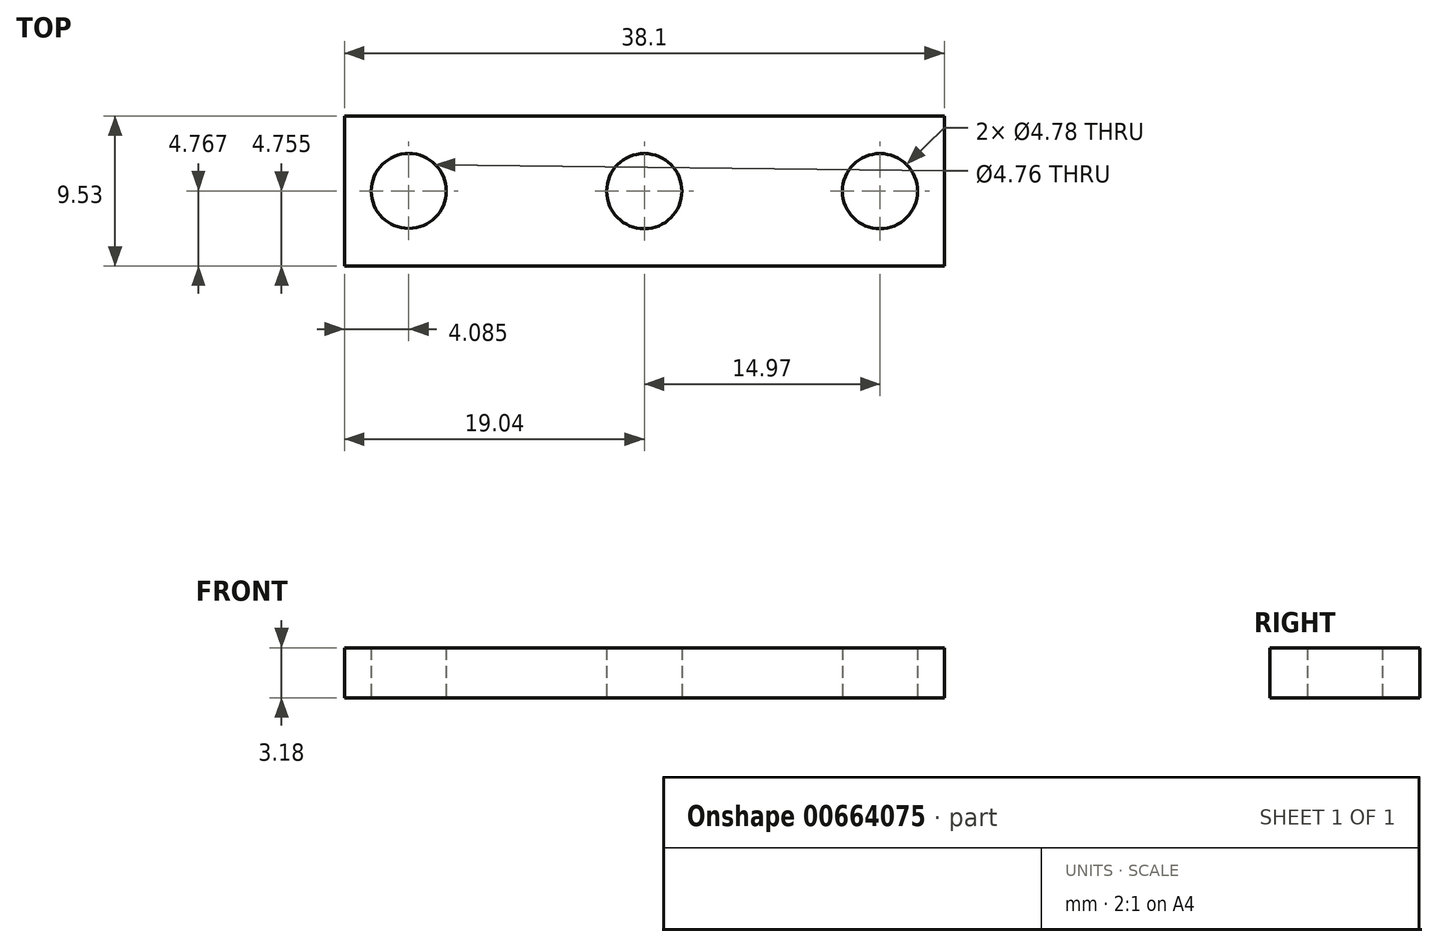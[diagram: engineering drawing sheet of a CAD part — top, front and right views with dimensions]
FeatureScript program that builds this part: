
annotation { "Feature Type Name" : "Feature", "Feature Type Description" : "" }
export const myFeature = defineFeature(function(context is Context, id is Id, definition is map)
    precondition{}
    {
        {
            var Q0;
            Q0=qCreatedBy(makeId("Top.planeOp"),FACE);
            var sketch = newSketch(context, id + "F0", { "sketchPlane" : qUnion([Q0])});
            skLineSegment(sketch, "E0.bottom", {"start": v(0, 0) * mm, "end": v(38.1, 0) * mm});
            skLineSegment(sketch, "E0.top", {"start": v(0, -9.53) * mm, "end": v(38.1, -9.53) * mm});
            skLineSegment(sketch, "E0.left", {"start": v(0, 0) * mm, "end": v(0, -9.53) * mm});
            skLineSegment(sketch, "E0.right", {"start": v(38.1, 0) * mm, "end": v(38.1, -9.53) * mm});
            skCircle(sketch, "E1", {"center": v(4.09, -4.76) * mm, "radius": 2.38 * mm});
            skPoint(sketch, "E1.centerSnap0", {"position": v(0, -4.76) * mm});
            skCircle(sketch, "E2", {"center": v(34.01, -4.78) * mm, "radius": 2.39 * mm});
            skCircle(sketch, "E3", {"center": v(19.04, -4.78) * mm, "radius": 2.39 * mm});
            skSolve(sketch);
        }
        {
            var Q0;
            Q0=makeQuery(id+"F0.imprint","IMPRINT",FACE,{"disambiguationData":[TD([[makeQuery(id+"F0.imprint","IMPRINT",EDGE,{"derivedFrom":sQuery(id+"F0.wireOp",EDGE,"E0.bottom")}),-1.0]])]});
            extrude(context, id + "F1", {"entities" : qUnion([Q0]), "depth" : 3.17 * mm, "offsetDistance" : 25.4 * mm});
        }
    });
